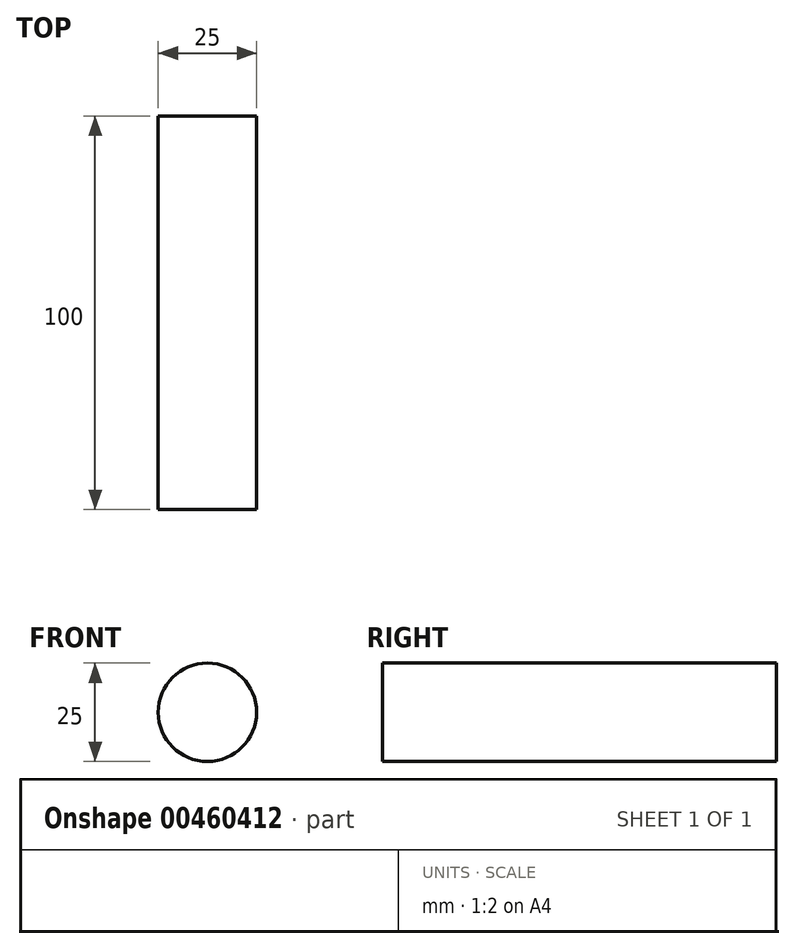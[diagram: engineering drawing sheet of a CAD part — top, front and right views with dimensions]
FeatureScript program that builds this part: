
annotation { "Feature Type Name" : "Feature", "Feature Type Description" : "" }
export const myFeature = defineFeature(function(context is Context, id is Id, definition is map)
    precondition{}
    {
        {
            var Q0;
            Q0=qCreatedBy(makeId("Front.planeOp"),FACE);
            var sketch = newSketch(context, id + "F0", { "sketchPlane" : qUnion([Q0])});
            skCircle(sketch, "E0", {"center": v(0, 0) * mm, "radius": 12.5 * mm});
            skSolve(sketch);
        }
        {
            var Q0;
            Q0 = qSketchRegion(id + "F0", true);
            extrude(context, id + "F1", {"entities" : qUnion([Q0]), "depth" : 100 * mm});
        }
    });
